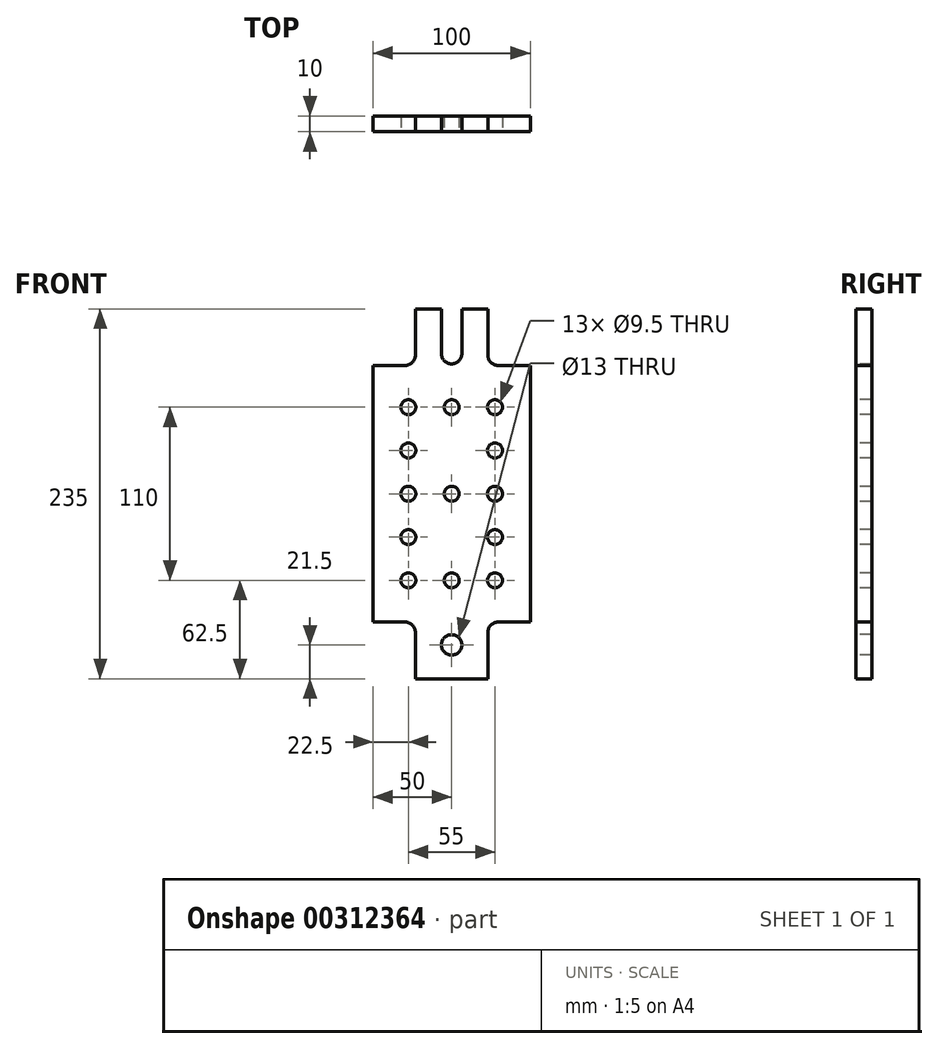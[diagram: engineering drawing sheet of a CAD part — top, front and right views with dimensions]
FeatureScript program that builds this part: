
annotation { "Feature Type Name" : "Feature", "Feature Type Description" : "" }
export const myFeature = defineFeature(function(context is Context, id is Id, definition is map)
    precondition{}
    {
        {
            var Q0;
            Q0=qCreatedBy(makeId("Front.planeOp"),FACE);
            var sketch = newSketch(context, id + "F0", { "sketchPlane" : qUnion([Q0])});
            skLineSegment(sketch, "E0", {"start": v(0, 0) * mm, "end": v(-23, 0) * mm});
            skLineSegment(sketch, "E1", {"start": v(-23, 0) * mm, "end": v(-23, 36) * mm});
            skLineSegment(sketch, "E2", {"start": v(-23, 36) * mm, "end": v(-50, 36) * mm});
            skLineSegment(sketch, "E3", {"start": v(-50, 36) * mm, "end": v(-50, 199) * mm});
            skLineSegment(sketch, "E4", {"start": v(-50, 199) * mm, "end": v(-23, 199) * mm});
            skLineSegment(sketch, "E5", {"start": v(-23, 199) * mm, "end": v(-23, 235) * mm});
            skLineSegment(sketch, "E6", {"start": v(-23, 235) * mm, "end": v(-6.5, 235) * mm});
            skLineSegment(sketch, "E7", {"start": v(-6.5, 235) * mm, "end": v(-6.5, 200) * mm});
            skLineSegment(sketch, "E8", {"start": v(-6.5, 200) * mm, "end": v(0, 200) * mm});
            skLineSegment(sketch, "E9", {"start": v(0, 200) * mm, "end": v(0, 0) * mm});
            skSolve(sketch);
        }
        {
            var Q0;
            Q0=makeQuery(id+"F0.imprint","IMPRINT",FACE,{"disambiguationData":[TD([[makeQuery(id+"F0.imprint","IMPRINT",EDGE,{"derivedFrom":sQuery(id+"F0.wireOp",EDGE,"E0")}),-1.0]])]});
            extrude(context, id + "F1", {"entities" : qUnion([Q0]), "depth" : 10 * mm});
        }
        {
            var Q0;
            Q0=makeQuery(id+"F1.opExtrude","CAP_FACE",FACE,{"disambiguationData":[OSD([sQuery(id+"F0.wireOp",EDGE,"E0"),sQuery(id+"F0.wireOp",EDGE,"E1"),sQuery(id+"F0.wireOp",EDGE,"E2"),sQuery(id+"F0.wireOp",EDGE,"E3"),sQuery(id+"F0.wireOp",EDGE,"E4"),sQuery(id+"F0.wireOp",EDGE,"E5"),sQuery(id+"F0.wireOp",EDGE,"E6"),sQuery(id+"F0.wireOp",EDGE,"E7"),sQuery(id+"F0.wireOp",EDGE,"E8"),sQuery(id+"F0.wireOp",EDGE,"E9")])],"isStart":false});
            var sketch = newSketch(context, id + "F2", { "sketchPlane" : qUnion([Q0])});
            skLineSegment(sketch, "E10", {"start": v(-27.5, 172.5) * mm, "end": v(-27.5, 62.5) * mm});
            skLineSegment(sketch, "E11", {"start": v(-27.5, 62.5) * mm, "end": v(0, 62.5) * mm});
            skLineSegment(sketch, "E12", {"start": v(0, 62.5) * mm, "end": v(0, 172.5) * mm});
            skLineSegment(sketch, "E13", {"start": v(0, 172.5) * mm, "end": v(-27.5, 172.5) * mm});
            skLineSegment(sketch, "E14", {"start": v(-27.5, 117.5) * mm, "end": v(0, 117.5) * mm});
            skLineSegment(sketch, "E15", {"start": v(-27.5, 145) * mm, "end": v(0, 145) * mm});
            skLineSegment(sketch, "E16", {"start": v(-27.5, 90) * mm, "end": v(0, 90) * mm});
            skSolve(sketch);
        }
        {
            var Q0;
            Q0=sQuery(id+"F2.wireOp",VERTEX,"E13.end");
            var Q1;
            Q1=sQuery(id+"F2.wireOp",VERTEX,"E15.start");
            var Q2;
            Q2=sQuery(id+"F2.wireOp",VERTEX,"E14.start");
            var Q3;
            Q3=sQuery(id+"F2.wireOp",VERTEX,"E16.start");
            var Q4;
            Q4=sQuery(id+"F2.wireOp",VERTEX,"E11.start");
            var Q5;
            Q5=sQuery(id+"F2.wireOp",VERTEX,"E12.start");
            var Q6;
            Q6=sQuery(id+"F2.wireOp",VERTEX,"E14.end");
            var Q7;
            Q7=sQuery(id+"F2.wireOp",VERTEX,"E12.end");
            var Q8;
            Q8=makeQuery(id+"F1.opExtrude","SWEPT_BODY",BODY,{"disambiguationData":[OSD([sQuery(id+"F0.wireOp",EDGE,"E0"),sQuery(id+"F0.wireOp",EDGE,"E1"),sQuery(id+"F0.wireOp",EDGE,"E2"),sQuery(id+"F0.wireOp",EDGE,"E3"),sQuery(id+"F0.wireOp",EDGE,"E4"),sQuery(id+"F0.wireOp",EDGE,"E5"),sQuery(id+"F0.wireOp",EDGE,"E6"),sQuery(id+"F0.wireOp",EDGE,"E7"),sQuery(id+"F0.wireOp",EDGE,"E8"),sQuery(id+"F0.wireOp",EDGE,"E9")])]});
            hole(context, id + "F3", {"style" : HoleStyle.SIMPLE, "endStyle" : HoleEndStyle.THROUGH, "holeDiameter" : 9.5 * mm, "tappedDepth" : 12 * mm, "tapClearance" : 3, "locations" : qUnion([Q0, Q1, Q2, Q3, Q4, Q5, Q6, Q7]), "scope" : qUnion([Q8])});
        }
        {
            var Q0;
            Q0=makeQuery(id+"F1.opExtrude","SWEPT_BODY",BODY,{"disambiguationData":[OSD([sQuery(id+"F0.wireOp",EDGE,"E0"),sQuery(id+"F0.wireOp",EDGE,"E1"),sQuery(id+"F0.wireOp",EDGE,"E2"),sQuery(id+"F0.wireOp",EDGE,"E3"),sQuery(id+"F0.wireOp",EDGE,"E4"),sQuery(id+"F0.wireOp",EDGE,"E5"),sQuery(id+"F0.wireOp",EDGE,"E6"),sQuery(id+"F0.wireOp",EDGE,"E7"),sQuery(id+"F0.wireOp",EDGE,"E8"),sQuery(id+"F0.wireOp",EDGE,"E9")])]});
            var Q1;
            {var subQ0=sQuery(id+"F0.wireOp",EDGE,"E9");var subQ1=sQuery(id+"F0.wireOp",EDGE,"E8");var subQ12=makeQuery(id+"F3.hole-6.opRevolve","SWEPT_FACE",FACE,{"disambiguationData":[OSD([sQuery(id+"F3.hole-6.sketch.wireOp",EDGE,"core_line_2")])]});var subQ13=makeQuery(id+"F1.opExtrude","SWEPT_FACE",FACE,{"disambiguationData":[OSD([subQ1])]});Q1=makeQuery(id+"F3.hole-7.boolean.opBoolean","SPLIT",FACE,{"disambiguationData":[TD([makeQuery(id+"F3.hole-6.boolean.opBoolean","COPY",FACE,{"derivedFrom":subQ12})])],"derivedFrom":makeQuery(id+"F3.hole-6.boolean.opBoolean","SPLIT",FACE,{"disambiguationData":[TD([subQ13])],"derivedFrom":makeQuery(id+"F3.hole-5.boolean.opBoolean","SPLIT",FACE,{"disambiguationData":[TD([subQ13])],"derivedFrom":makeQuery(id+"F1.opExtrude","SWEPT_FACE",FACE,{"disambiguationData":[OSD([subQ0])]})})})});}
            mirror(context, id + "F4", {"operationType" : NewBodyOperationType.ADD, "entities" : qUnion([Q0]), "mirrorPlane" : qUnion([Q1])});
        }
        {
            var Q0;
            {var subQ0=makeQuery(id+"F1.opExtrude","CAP_FACE",FACE,{"disambiguationData":[OSD([sQuery(id+"F0.wireOp",EDGE,"E0"),sQuery(id+"F0.wireOp",EDGE,"E1"),sQuery(id+"F0.wireOp",EDGE,"E2"),sQuery(id+"F0.wireOp",EDGE,"E3"),sQuery(id+"F0.wireOp",EDGE,"E4"),sQuery(id+"F0.wireOp",EDGE,"E5"),sQuery(id+"F0.wireOp",EDGE,"E6"),sQuery(id+"F0.wireOp",EDGE,"E7"),sQuery(id+"F0.wireOp",EDGE,"E8"),sQuery(id+"F0.wireOp",EDGE,"E9")])],"isStart":false});Q0=makeQuery(id+"F4.boolean.opBoolean","MERGE",FACE,{"derivedFrom":[subQ0,makeQuery(id+"F4.opPattern","COPY",FACE,{"derivedFrom":subQ0,"instanceName":"1"})]});}
            var sketch = newSketch(context, id + "F5", { "sketchPlane" : qUnion([Q0])});
            skSolve(sketch);
        }
        {
            var Q0;
            {var subQ9=makeQuery(id+"F1.opExtrude","CAP_EDGE",EDGE,{"disambiguationData":[OSD([sQuery(id+"F0.wireOp",EDGE,"E1")])],"isStart":false});Q0=makeQuery(id+"F5.imprint","IMPRINT",FACE,{"disambiguationData":[TD([[makeQuery(id+"F5.imprint","IMPRINT",EDGE,{"derivedFrom":subQ9}),-1.0]])]});}
            var sketch = newSketch(context, id + "F6", { "sketchPlane" : qUnion([Q0])});
            skPoint(sketch, "E17", {"position": v(0, 21.5) * mm});
            skSolve(sketch);
        }
        {
            var Q0;
            Q0=sQuery(id+"F6.wireOp",VERTEX,"E17");
            var Q1;
            Q1=makeQuery(id+"F1.opExtrude","SWEPT_BODY",BODY,{"disambiguationData":[OSD([sQuery(id+"F0.wireOp",EDGE,"E0"),sQuery(id+"F0.wireOp",EDGE,"E1"),sQuery(id+"F0.wireOp",EDGE,"E2"),sQuery(id+"F0.wireOp",EDGE,"E3"),sQuery(id+"F0.wireOp",EDGE,"E4"),sQuery(id+"F0.wireOp",EDGE,"E5"),sQuery(id+"F0.wireOp",EDGE,"E6"),sQuery(id+"F0.wireOp",EDGE,"E7"),sQuery(id+"F0.wireOp",EDGE,"E8"),sQuery(id+"F0.wireOp",EDGE,"E9")])]});
            hole(context, id + "F7", {"style" : HoleStyle.SIMPLE, "endStyle" : HoleEndStyle.THROUGH, "holeDiameter" : 13 * mm, "tappedDepth" : 12 * mm, "tapClearance" : 3, "locations" : qUnion([Q0]), "scope" : qUnion([Q1])});
        }
        {
            var Q0;
            Q0=makeQuery(id+"F1.opExtrude","SWEPT_EDGE",EDGE,{"disambiguationData":[OSD([sQuery(id+"F0.wireOp",EDGE,"E7"),sQuery(id+"F0.wireOp",EDGE,"E8")])]});
            var Q1;
            Q1=makeQuery(id+"F4.opPattern","COPY",EDGE,{"derivedFrom":makeQuery(id+"F1.opExtrude","SWEPT_EDGE",EDGE,{"disambiguationData":[OSD([sQuery(id+"F0.wireOp",EDGE,"E7"),sQuery(id+"F0.wireOp",EDGE,"E8")])]}),"instanceName":"1"});
            fillet(context, id + "F8", {"entities" : qUnion([Q0, Q1]), "radius" : 6.5 * mm, "tangentPropagation" : true, "allowEdgeOverflow" : false});
        }
        {
            var Q0;
            Q0=makeQuery(id+"F4.opPattern","COPY",EDGE,{"derivedFrom":makeQuery(id+"F1.opExtrude","SWEPT_EDGE",EDGE,{"disambiguationData":[OSD([sQuery(id+"F0.wireOp",EDGE,"E4"),sQuery(id+"F0.wireOp",EDGE,"E5")])]}),"instanceName":"1"});
            var Q1;
            Q1=makeQuery(id+"F1.opExtrude","SWEPT_EDGE",EDGE,{"disambiguationData":[OSD([sQuery(id+"F0.wireOp",EDGE,"E4"),sQuery(id+"F0.wireOp",EDGE,"E5")])]});
            var Q2;
            Q2=makeQuery(id+"F4.opPattern","COPY",EDGE,{"derivedFrom":makeQuery(id+"F1.opExtrude","SWEPT_EDGE",EDGE,{"disambiguationData":[OSD([sQuery(id+"F0.wireOp",EDGE,"E1"),sQuery(id+"F0.wireOp",EDGE,"E2")])]}),"instanceName":"1"});
            var Q3;
            Q3=makeQuery(id+"F1.opExtrude","SWEPT_EDGE",EDGE,{"disambiguationData":[OSD([sQuery(id+"F0.wireOp",EDGE,"E1"),sQuery(id+"F0.wireOp",EDGE,"E2")])]});
            fillet(context, id + "F9", {"entities" : qUnion([Q0, Q1, Q2, Q3]), "radius" : 6.5 * mm, "tangentPropagation" : true, "allowEdgeOverflow" : false});
        }
    });
